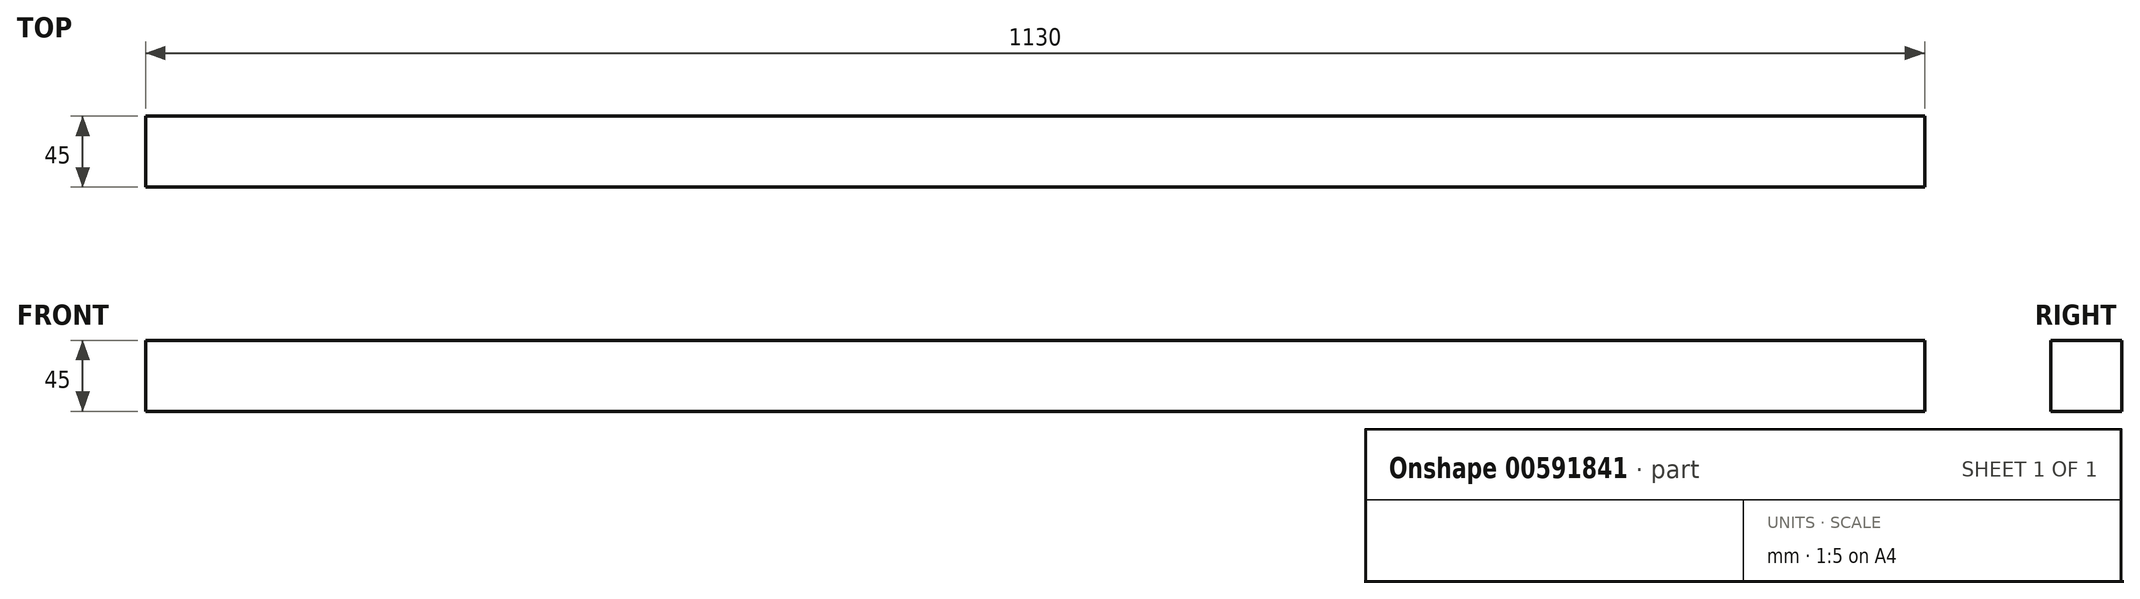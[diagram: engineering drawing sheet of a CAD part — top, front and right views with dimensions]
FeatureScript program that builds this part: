
annotation { "Feature Type Name" : "Feature", "Feature Type Description" : "" }
export const myFeature = defineFeature(function(context is Context, id is Id, definition is map)
    precondition{}
    {
        {
            var Q0;
            Q0=qCreatedBy(makeId("Right.planeOp"),FACE);
            var sketch = newSketch(context, id + "F0", { "sketchPlane" : qUnion([Q0])});
            skLineSegment(sketch, "E0.bottom", {"start": v(0, 0) * mm, "end": v(45, 0) * mm});
            skLineSegment(sketch, "E0.top", {"start": v(0, 45) * mm, "end": v(45, 45) * mm});
            skLineSegment(sketch, "E0.left", {"start": v(0, 0) * mm, "end": v(0, 45) * mm});
            skLineSegment(sketch, "E0.right", {"start": v(45, 0) * mm, "end": v(45, 45) * mm});
            skSolve(sketch);
        }
        {
            var Q0;
            Q0=makeQuery(id+"F0.imprint","IMPRINT",FACE,{"disambiguationData":[TD([[makeQuery(id+"F0.imprint","IMPRINT",EDGE,{"derivedFrom":sQuery(id+"F0.wireOp",EDGE,"E0.bottom")}),1.0]])]});
            extrude(context, id + "F1", {"entities" : qUnion([Q0]), "depth" : 1130 * mm, "offsetDistance" : 25 * mm});
        }
    });
